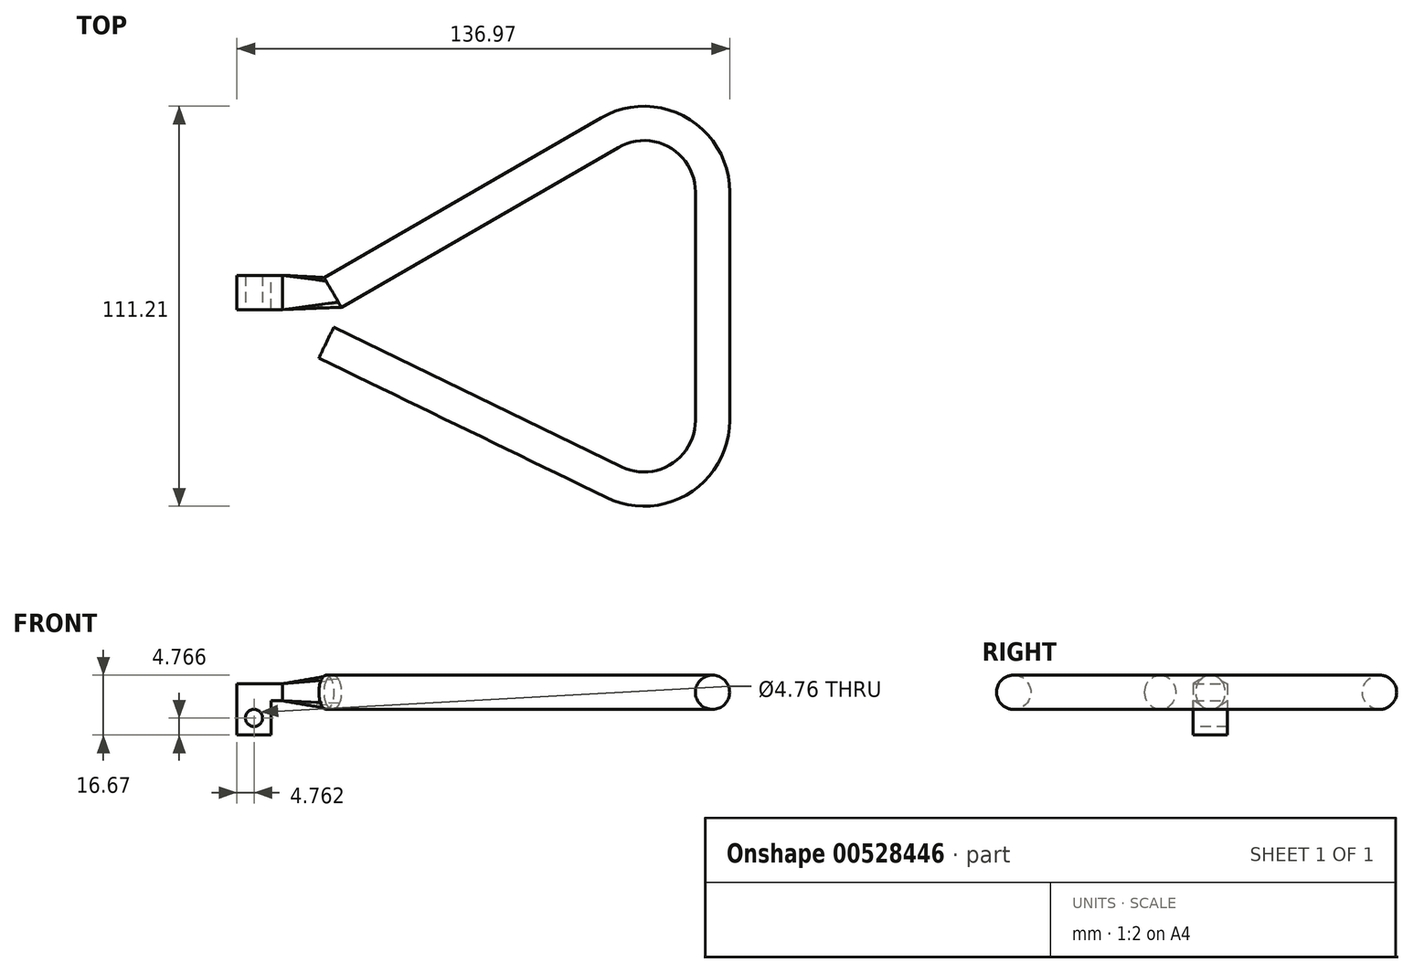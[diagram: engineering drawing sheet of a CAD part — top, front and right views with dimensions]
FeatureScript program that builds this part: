
annotation { "Feature Type Name" : "Feature", "Feature Type Description" : "" }
export const myFeature = defineFeature(function(context is Context, id is Id, definition is map)
    precondition{}
    {
        {
            var Q0;
            Q0=qCreatedBy(makeId("Top.planeOp"),FACE);
            var sketch = newSketch(context, id + "F0", { "sketchPlane" : qUnion([Q0])});
            skLineSegment(sketch, "E0", {"start": v(12.16, -5.9) * mm, "end": v(92.14, -44.72) * mm});
            skLineSegment(sketch, "E1", {"start": v(119.51, -27.58) * mm, "end": v(119.51, 36) * mm});
            skLineSegment(sketch, "E2", {"start": v(90.94, 52.5) * mm, "end": v(13.95, 8.05) * mm});
            skPoint(sketch, "E3.visualSharp", {"position": v(119.51, 69) * mm});
            skArc(sketch, "E3.filletArc", {"start": v(119.51, 36) * mm, "mid": v(109.99, 52.5) * mm, "end": v(90.94, 52.5) * mm});
            skPoint(sketch, "E4.visualSharp", {"position": v(119.51, -58) * mm});
            skArc(sketch, "E4.filletArc", {"start": v(92.14, -44.72) * mm, "mid": v(110.57, -43.73) * mm, "end": v(119.51, -27.58) * mm});
            skPoint(sketch, "E5", {"position": v(12.16, -5.9) * mm});
            skLineSegment(sketch, "E6", {"start": v(10.78, -8.76) * mm, "end": v(13.55, -3.05) * mm});
            skLineSegment(sketch, "E7", {"start": v(12.36, 10.8) * mm, "end": v(15.53, 5.3) * mm});
            skSolve(sketch);
        }
        {
            var Q0;
            Q0=sQuery(id+"F0.wireOp",EDGE,"E6");
            var Q1;
            Q1=sQuery(id+"F0.wireOp",EDGE,"E0");
            cPlane(context, id + "F1", {"entities" : qUnion([Q0, Q1]), "cplaneType" : CPlaneType.LINE_ANGLE, "offset" : 25.4 * mm, "angle" : 90 * degree, "width" : 152.4 * mm, "height" : 152.4 * mm});
        }
        {
            var Q0;
            Q0=qCreatedBy(id+"F1.planeOp",FACE);
            var sketch = newSketch(context, id + "F2", { "sketchPlane" : qUnion([Q0])});
            skCircle(sketch, "E8", {"center": v(0, 0) * mm, "radius": 4.76 * mm});
            skSolve(sketch);
        }
        {
            var Q0;
            Q0=makeQuery(id+"F2.imprint","IMPRINT",FACE,{"disambiguationData":[TD([[makeQuery(id+"F2.imprint","IMPRINT",EDGE,{"derivedFrom":sQuery(id+"F2.wireOp",EDGE,"E8")}),1.0]])]});
            var Q1;
            Q1=sQuery(id+"F0.wireOp",EDGE,"E0");
            var Q2;
            Q2=sQuery(id+"F0.wireOp",EDGE,"E4.filletArc");
            var Q3;
            Q3=sQuery(id+"F0.wireOp",EDGE,"E1");
            var Q4;
            Q4=sQuery(id+"F0.wireOp",EDGE,"E3.filletArc");
            var Q5;
            Q5=sQuery(id+"F0.wireOp",EDGE,"E2");
            sweep(context, id + "F3", {"profiles" : qUnion([Q0]), "path" : qUnion([Q1, Q2, Q3, Q4, Q5])});
        }
        {
            var Q0;
            Q0=qCreatedBy(makeId("Right.planeOp"),FACE);
            var sketch = newSketch(context, id + "F4", { "sketchPlane" : qUnion([Q0])});
            skLineSegment(sketch, "E9.bottom", {"start": v(3.29, 2.38) * mm, "end": v(12.81, 2.38) * mm});
            skLineSegment(sketch, "E9.top", {"start": v(3.29, -2.38) * mm, "end": v(12.81, -2.38) * mm});
            skLineSegment(sketch, "E9.left", {"start": v(3.29, 2.38) * mm, "end": v(3.29, -2.38) * mm});
            skLineSegment(sketch, "E9.right", {"start": v(12.81, 2.38) * mm, "end": v(12.81, -2.38) * mm});
            skPoint(sketch, "E9.middle", {"position": v(8.05, 0) * mm});
            skLineSegment(sketch, "E10", {"start": v(8.05, 15.41) * mm, "end": v(8.05, -15.41) * mm, "construction": true});
            skSolve(sketch);
        }
        {
            var Q1;
            Q1=makeQuery(id+"F3.opSweep","CAP_FACE",FACE,{"disambiguationData":[OSD([sQuery(id+"F0.wireOp",VERTEX,"E2.end"),sQuery(id+"F2.wireOp",EDGE,"E8")])],"isStart":false});
            var Q2;
            Q2 = qSketchRegion(id + "F4", true);
            loft(context, id + "F5", {"operationType" : NewBodyOperationType.ADD, "sheetProfilesArray" : [{ "sheetProfileEntities" : qUnion([Q1]) }, { "sheetProfileEntities" : qUnion([Q2]) }]});
        }
        {
            var Q0;
            Q0=makeQuery(id+"F5.opLoft","CAP_FACE",FACE,{"disambiguationData":[OSD([makeQuery(id+"F4.imprint","IMPRINT",FACE,{"disambiguationData":[TD([[makeQuery(id+"F4.imprint","IMPRINT",EDGE,{"derivedFrom":sQuery(id+"F4.wireOp",EDGE,"E9.bottom")}),-1.0]])]})])],"isStart":true});
            var sketch = newSketch(context, id + "F6", { "sketchPlane" : qUnion([Q0])});
            skLineSegment(sketch, "E11.0", {"start": v(-3.29, 2.38) * mm, "end": v(-12.81, 2.38) * mm});
            skLineSegment(sketch, "E11.1", {"start": v(-3.29, -2.38) * mm, "end": v(-3.29, 2.38) * mm});
            skLineSegment(sketch, "E11.2", {"start": v(-12.81, -2.38) * mm, "end": v(-3.29, -2.38) * mm});
            skLineSegment(sketch, "E11.3", {"start": v(-12.81, 2.38) * mm, "end": v(-12.81, -2.38) * mm});
            skSolve(sketch);
        }
        {
            var Q0;
            Q0 = qSketchRegion(id + "F6", true);
            extrude(context, id + "F7", {"entities" : qUnion([Q0]), "operationType" : NewBodyOperationType.ADD, "depth" : 12.7 * mm, "offsetDistance" : 25.4 * mm});
        }
        {
            var Q0;
            Q0=makeQuery(id+"F7.opExtrude","SWEPT_FACE",FACE,{"disambiguationData":[OSD([sQuery(id+"F6.wireOp",EDGE,"E11.2")])]});
            var sketch = newSketch(context, id + "F8", { "sketchPlane" : qUnion([Q0])});
            skPoint(sketch, "E12.0", {"position": v(-12.7, -3.29) * mm});
            skPoint(sketch, "E13.0", {"position": v(-12.7, -12.81) * mm});
            skLineSegment(sketch, "E14.bottom", {"start": v(-12.7, -3.29) * mm, "end": v(-3.18, -3.29) * mm});
            skLineSegment(sketch, "E14.top", {"start": v(-12.7, -12.81) * mm, "end": v(-3.18, -12.81) * mm});
            skLineSegment(sketch, "E14.left", {"start": v(-12.7, -3.29) * mm, "end": v(-12.7, -12.81) * mm});
            skLineSegment(sketch, "E14.right", {"start": v(-3.18, -3.29) * mm, "end": v(-3.17, -12.81) * mm});
            skSolve(sketch);
        }
        {
            var Q0;
            Q0=makeQuery(id+"F8.imprint","IMPRINT",FACE,{"disambiguationData":[TD([[makeQuery(id+"F8.imprint","IMPRINT",EDGE,{"derivedFrom":sQuery(id+"F8.wireOp",EDGE,"E14.bottom")}),1.0]])]});
            extrude(context, id + "F9", {"entities" : qUnion([Q0]), "operationType" : NewBodyOperationType.ADD, "depth" : 9.52 * mm, "offsetDistance" : 25.4 * mm});
        }
        {
            var Q0;
            Q0=makeQuery(id+"F9.boolean.opBoolean","MERGE",FACE,{"derivedFrom":[makeQuery(id+"F7.opExtrude","SWEPT_FACE",FACE,{"disambiguationData":[OSD([sQuery(id+"F6.wireOp",EDGE,"E11.1")])]}),makeQuery(id+"F9.opExtrude","SWEPT_FACE",FACE,{"disambiguationData":[OSD([sQuery(id+"F8.wireOp",EDGE,"E14.bottom")])]})]});
            var sketch = newSketch(context, id + "F10", { "sketchPlane" : qUnion([Q0])});
            skPoint(sketch, "E15.0", {"position": v(-7.94, -11.9) * mm});
            skLineSegment(sketch, "E16", {"start": v(-7.94, -11.9) * mm, "end": v(-7.94, 2.38) * mm, "construction": true});
            skPoint(sketch, "E17.0", {"position": v(-3.18, -7.14) * mm});
            skLineSegment(sketch, "E18", {"start": v(-3.18, -7.14) * mm, "end": v(-12.7, -7.14) * mm, "construction": true});
            skPoint(sketch, "E19", {"position": v(-7.94, -7.14) * mm});
            skCircle(sketch, "E20", {"center": v(-7.94, -7.14) * mm, "radius": 2.38 * mm});
            skSolve(sketch);
        }
        {
            var Q0;
            Q0=makeQuery(id+"F10.imprint","IMPRINT",FACE,{"disambiguationData":[TD([[makeQuery(id+"F10.imprint","IMPRINT",EDGE,{"derivedFrom":sQuery(id+"F10.wireOp",EDGE,"E20")}),1.0]])]});
            extrude(context, id + "F11", {"entities" : qUnion([Q0]), "operationType" : NewBodyOperationType.REMOVE, "endBound" : BoundingType.THROUGH_ALL, "oppositeDirection" : true, "depth" : 25.4 * mm, "offsetDistance" : 25.4 * mm});
        }
    });
